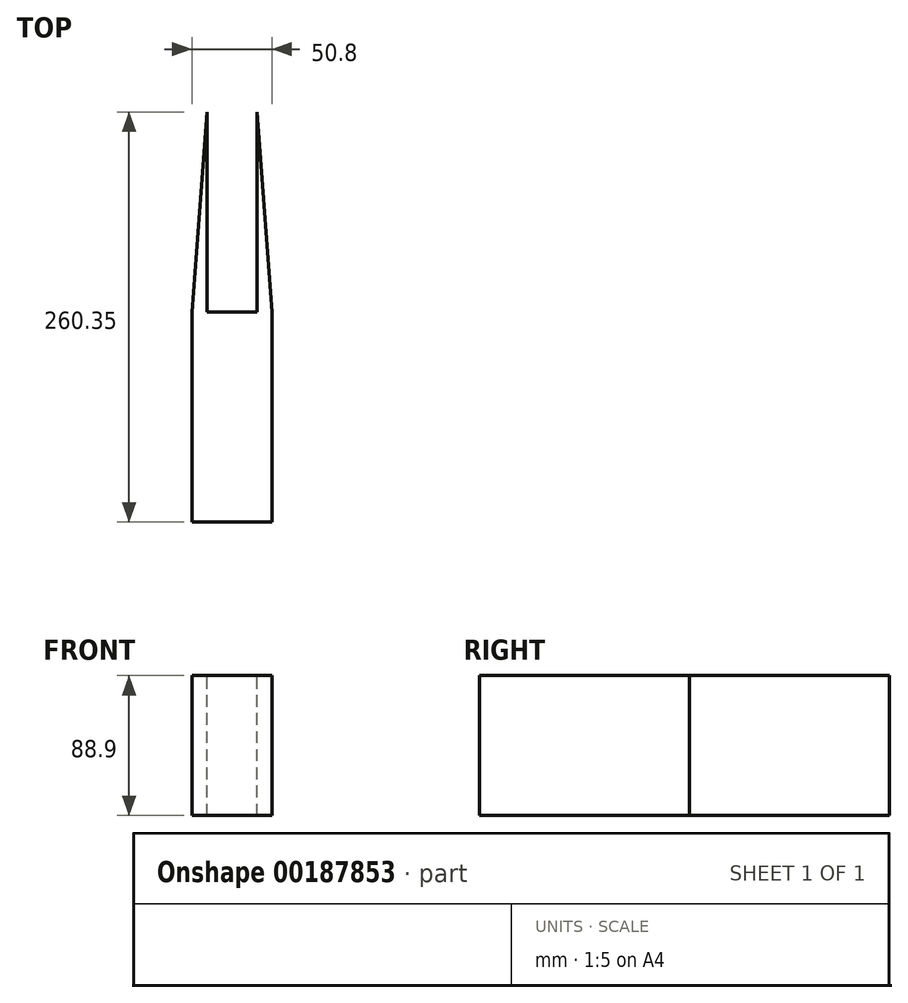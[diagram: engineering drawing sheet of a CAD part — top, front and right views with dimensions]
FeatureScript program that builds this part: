
annotation { "Feature Type Name" : "Feature", "Feature Type Description" : "" }
export const myFeature = defineFeature(function(context is Context, id is Id, definition is map)
    precondition{}
    {
        {
            var Q0;
            Q0=qCreatedBy(makeId("Top.planeOp"),FACE);
            var sketch = newSketch(context, id + "F0", { "sketchPlane" : qUnion([Q0])});
            skLineSegment(sketch, "E0.bottom", {"start": v(-25.4, 0) * mm, "end": v(25.4, 0) * mm});
            skLineSegment(sketch, "E0.top", {"start": v(-25.4, -133.35) * mm, "end": v(25.4, -133.35) * mm});
            skLineSegment(sketch, "E0.left", {"start": v(-25.4, 0) * mm, "end": v(-25.4, -133.35) * mm});
            skLineSegment(sketch, "E0.right", {"start": v(25.4, 0) * mm, "end": v(25.4, -133.35) * mm});
            skPoint(sketch, "E0.middle", {"position": v(0, -66.68) * mm});
            skLineSegment(sketch, "E1.bottom", {"start": v(-15.88, 0) * mm, "end": v(15.87, 0) * mm});
            skLineSegment(sketch, "E1.top", {"start": v(-15.88, 127) * mm, "end": v(15.87, 127) * mm});
            skLineSegment(sketch, "E1.left", {"start": v(-15.88, 0) * mm, "end": v(-15.88, 127) * mm});
            skLineSegment(sketch, "E1.right", {"start": v(15.87, 0) * mm, "end": v(15.87, 127) * mm});
            skPoint(sketch, "E1.middle", {"position": v(0, 63.5) * mm});
            skLineSegment(sketch, "E2", {"start": v(-15.88, 127) * mm, "end": v(-25.4, 0) * mm});
            skLineSegment(sketch, "E3", {"start": v(25.4, 0) * mm, "end": v(15.87, 127) * mm});
            skSolve(sketch);
        }
        {
            var Q0;
            Q0=makeQuery(id+"F0.imprint","IMPRINT",FACE,{"disambiguationData":[TD([[makeQuery(id+"F0.imprint","IMPRINT",EDGE,{"derivedFrom":sQuery(id+"F0.wireOp",EDGE,"E1.bottom")}),1.0]])]});
            var Q1;
            Q1=makeQuery(id+"F0.imprint","IMPRINT",FACE,{"disambiguationData":[TD([[makeQuery(id+"F0.imprint","IMPRINT",EDGE,{"derivedFrom":sQuery(id+"F0.wireOp",EDGE,"E0.top")}),1.0]])]});
            var Q2;
            {var subQ2=sQuery(id+"F0.wireOp",EDGE,"E1.right");Q2=makeQuery(id+"F0.imprint","IMPRINT",FACE,{"disambiguationData":[TD([[makeQuery(id+"F0.imprint","IMPRINT",EDGE,{"derivedFrom":subQ2}),-1.0]])]});}
            var Q3;
            {var subQ2=sQuery(id+"F0.wireOp",EDGE,"E1.left");Q3=makeQuery(id+"F0.imprint","IMPRINT",FACE,{"disambiguationData":[TD([[makeQuery(id+"F0.imprint","IMPRINT",EDGE,{"derivedFrom":subQ2}),1.0]])]});}
            extrude(context, id + "F1", {"entities" : qUnion([Q0, Q1, Q2, Q3]), "oppositeDirection" : true, "depth" : 88.9 * mm});
        }
    });
